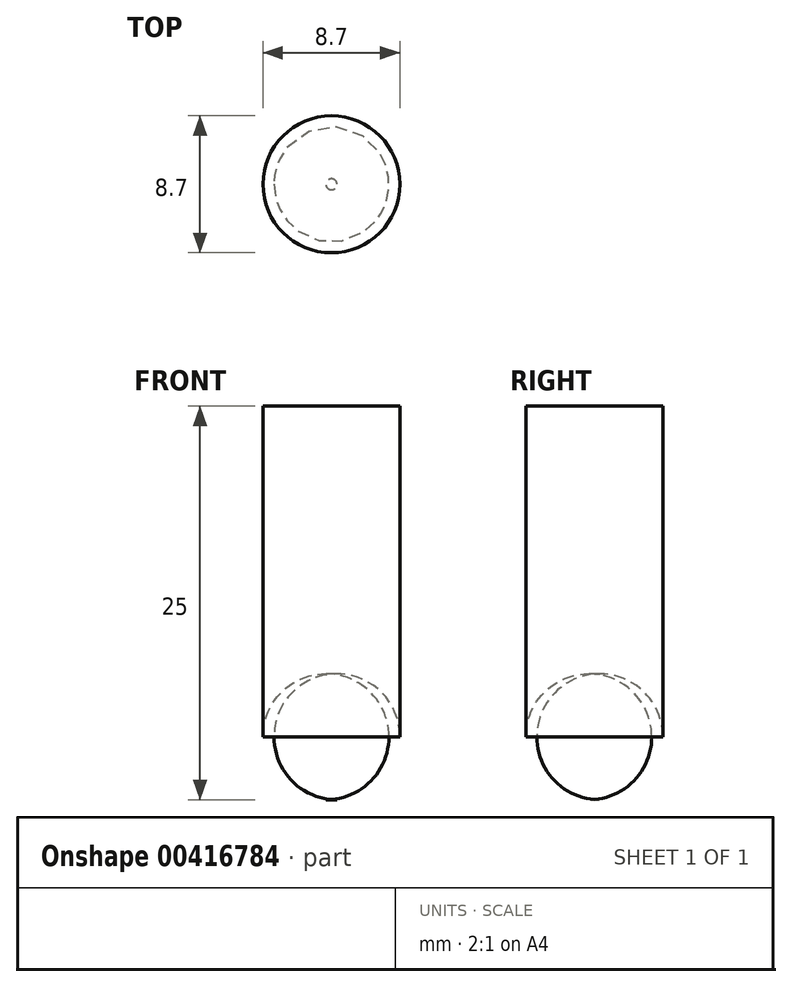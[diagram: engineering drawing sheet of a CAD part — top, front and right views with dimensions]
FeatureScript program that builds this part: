
annotation { "Feature Type Name" : "Feature", "Feature Type Description" : "" }
export const myFeature = defineFeature(function(context is Context, id is Id, definition is map)
    precondition{}
    {
        {
            var Q0;
            Q0=qCreatedBy(makeId("Top.planeOp"),FACE);
            var sketch = newSketch(context, id + "F0", { "sketchPlane" : qUnion([Q0])});
            skCircle(sketch, "E0", {"center": v(-55.14, -24.87) * mm, "radius": 4.35 * mm});
            skSolve(sketch);
        }
        {
            var Q0;
            Q0=qSketchRegion(id+"F0",true);
            extrude(context, id + "F1", {"entities" : qUnion([Q0]), "depth" : 25 * mm});
        }
        {
            var Q0;
            Q0=makeQuery(id+"F1.opExtrude","CAP_EDGE",EDGE,{"disambiguationData":[OSD([sQuery(id+"F0.wireOp",EDGE,"E0")])],"isStart":true});
            fillet(context, id + "F2", {"entities" : qUnion([Q0]), "radius" : 4 * mm, "tangentPropagation" : true, "allowEdgeOverflow" : false});
        }
    });
